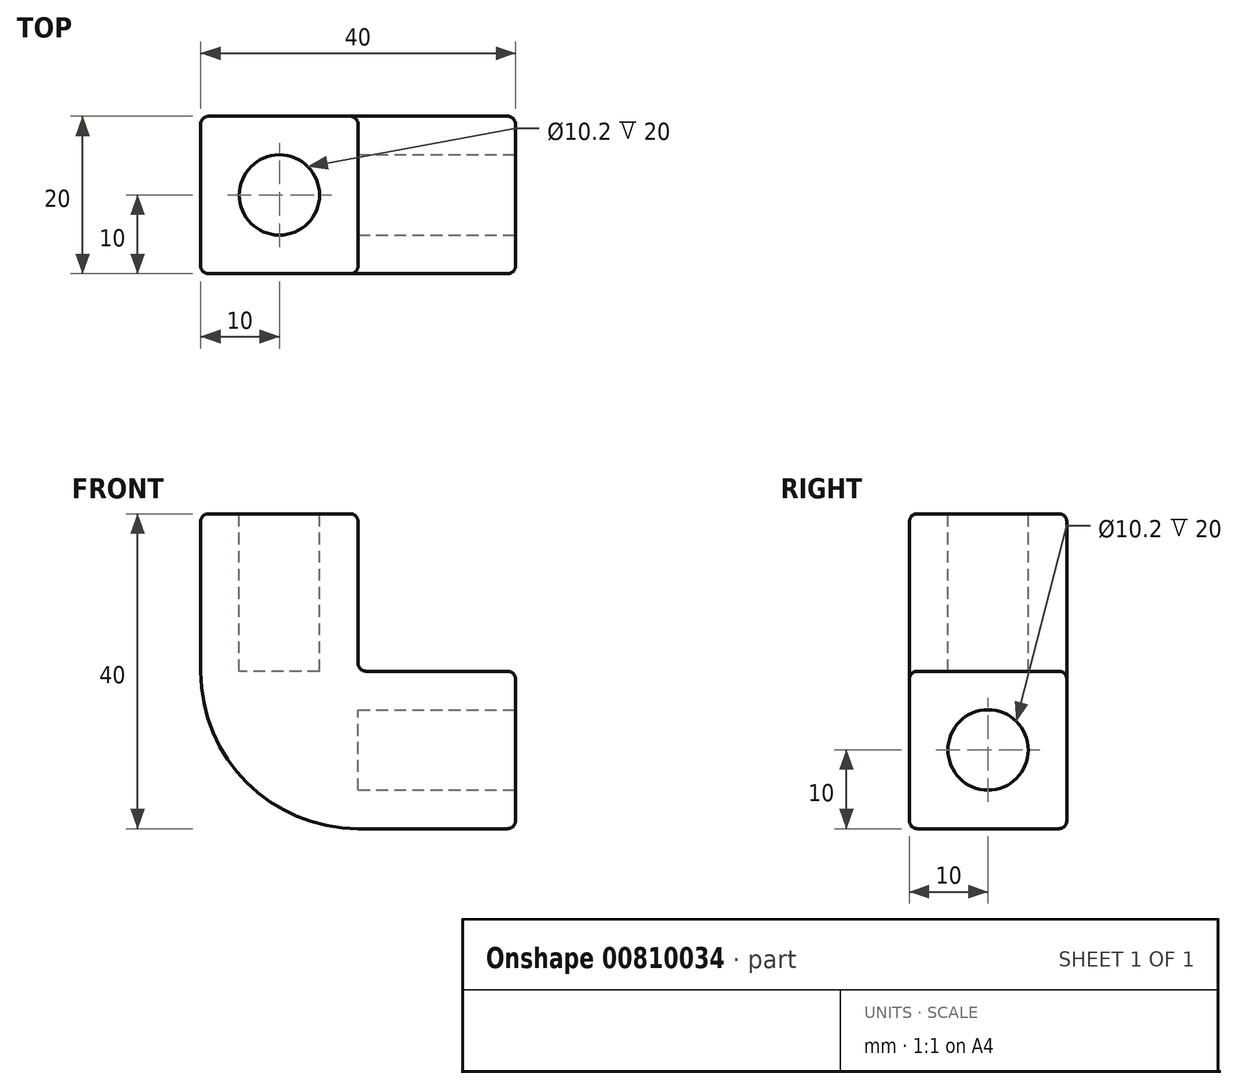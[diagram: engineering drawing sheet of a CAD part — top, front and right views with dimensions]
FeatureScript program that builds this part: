
annotation { "Feature Type Name" : "Feature", "Feature Type Description" : "" }
export const myFeature = defineFeature(function(context is Context, id is Id, definition is map)
    precondition{}
    {
        {
            var Q0;
            Q0=qCreatedBy(makeId("Front.planeOp"),FACE);
            var sketch = newSketch(context, id + "F0", { "sketchPlane" : qUnion([Q0])});
            skLineSegment(sketch, "E0.bottom", {"start": v(0, 0) * mm, "end": v(-20, 0) * mm});
            skLineSegment(sketch, "E0.top", {"start": v(0, 40) * mm, "end": v(-20, 40) * mm});
            skLineSegment(sketch, "E0.left", {"start": v(0, 0) * mm, "end": v(0, 40) * mm});
            skLineSegment(sketch, "E0.right", {"start": v(-20, 0) * mm, "end": v(-20, 40) * mm});
            skLineSegment(sketch, "E1.bottom", {"start": v(-20, 0) * mm, "end": v(20, 0) * mm});
            skLineSegment(sketch, "E1.top", {"start": v(-20, 20) * mm, "end": v(20, 20) * mm});
            skLineSegment(sketch, "E1.left", {"start": v(-20, 0) * mm, "end": v(-20, 20) * mm});
            skLineSegment(sketch, "E1.right", {"start": v(20, 0) * mm, "end": v(20, 20) * mm});
            skLineSegment(sketch, "E2", {"start": v(20, 20) * mm, "end": v(0, 40) * mm});
            skLineSegment(sketch, "E3", {"start": v(0, 0) * mm, "end": v(-20, 20) * mm});
            skArc(sketch, "E4", {"start": v(-20, 20) * mm, "mid": v(-14.14, 5.86) * mm, "end": v(0, 0) * mm});
            skArc(sketch, "E5", {"start": v(0, 40) * mm, "mid": v(5.86, 25.86) * mm, "end": v(20, 20) * mm});
            skSolve(sketch);
        }
        {
            var Q0;
            {var subQ0=sQuery(id+"F0.wireOp",EDGE,"E0.top");Q0=makeQuery(id+"F0.imprint","IMPRINT",FACE,{"disambiguationData":[TD([[makeQuery(id+"F0.imprint","IMPRINT",EDGE,{"derivedFrom":subQ0}),1.0]])]});}
            var Q1;
            {var subQ5=sQuery(id+"F0.wireOp",EDGE,"E1.right");Q1=makeQuery(id+"F0.imprint","IMPRINT",FACE,{"disambiguationData":[TD([[makeQuery(id+"F0.imprint","IMPRINT",EDGE,{"derivedFrom":subQ5}),1.0]])]});}
            var Q2;
            {var subQ0=sQuery(id+"F0.wireOp",EDGE,"E3");Q2=makeQuery(id+"F0.imprint","IMPRINT",FACE,{"disambiguationData":[TD([[makeQuery(id+"F0.imprint","IMPRINT",EDGE,{"derivedFrom":subQ0}),-1.0]])]});}
            var Q3;
            Q3=makeQuery(id+"F0.imprint","IMPRINT",FACE,{"disambiguationData":[TD([[makeQuery(id+"F0.imprint","IMPRINT",EDGE,{"derivedFrom":sQuery(id+"F0.wireOp",EDGE,"E3")}),1.0]])]});
            extrude(context, id + "F1", {"entities" : qUnion([Q0, Q1, Q2, Q3]), "depth" : 20 * mm, "offsetDistance" : 25 * mm});
        }
        {
            var Q0;
            Q0=makeQuery(id+"F1.opExtrude","CAP_EDGE",EDGE,{"disambiguationData":[OSD([sQuery(id+"F0.wireOp",EDGE,"E0.left")])],"isStart":false});
            var Q1;
            Q1=makeQuery(id+"F1.opExtrude","SWEPT_EDGE",EDGE,{"disambiguationData":[OSD([sQuery(id+"F0.wireOp",EDGE,"E0.top"),sQuery(id+"F0.wireOp",EDGE,"E0.left")])]});
            var Q2;
            Q2=makeQuery(id+"F1.opExtrude","CAP_EDGE",EDGE,{"disambiguationData":[OSD([sQuery(id+"F0.wireOp",EDGE,"E0.top")])],"isStart":false});
            var Q3;
            Q3=makeQuery(id+"F1.opExtrude","SWEPT_EDGE",EDGE,{"disambiguationData":[OSD([sQuery(id+"F0.wireOp",EDGE,"E0.top"),sQuery(id+"F0.wireOp",EDGE,"E0.right")])]});
            var Q4;
            Q4=makeQuery(id+"F1.opExtrude","CAP_EDGE",EDGE,{"disambiguationData":[OSD([sQuery(id+"F0.wireOp",EDGE,"E1.top")])],"isStart":false});
            var Q5;
            Q5=makeQuery(id+"F1.opExtrude","CAP_EDGE",EDGE,{"disambiguationData":[OSD([sQuery(id+"F0.wireOp",EDGE,"E1.top")])],"isStart":true});
            var Q6;
            Q6=makeQuery(id+"F1.opExtrude","SWEPT_EDGE",EDGE,{"disambiguationData":[OSD([sQuery(id+"F0.wireOp",EDGE,"E1.top"),sQuery(id+"F0.wireOp",EDGE,"E1.right")])]});
            var Q7;
            Q7=makeQuery(id+"F1.opExtrude","CAP_EDGE",EDGE,{"disambiguationData":[OSD([sQuery(id+"F0.wireOp",EDGE,"E1.right")])],"isStart":false});
            var Q8;
            Q8=makeQuery(id+"F1.opExtrude","CAP_EDGE",EDGE,{"disambiguationData":[OSD([sQuery(id+"F0.wireOp",EDGE,"E1.right")])],"isStart":true});
            var Q9;
            Q9=makeQuery(id+"F1.opExtrude","SWEPT_EDGE",EDGE,{"disambiguationData":[OSD([sQuery(id+"F0.wireOp",EDGE,"E1.bottom"),sQuery(id+"F0.wireOp",EDGE,"E1.right")])]});
            var Q10;
            Q10=makeQuery(id+"F1.opExtrude","CAP_EDGE",EDGE,{"disambiguationData":[OSD([sQuery(id+"F0.wireOp",EDGE,"E1.bottom")])],"isStart":false});
            var Q11;
            Q11=makeQuery(id+"F1.opExtrude","CAP_EDGE",EDGE,{"disambiguationData":[OSD([sQuery(id+"F0.wireOp",EDGE,"E0.right"),sQuery(id+"F0.wireOp",EDGE,"E1.left")])],"isStart":false});
            var Q12;
            Q12=makeQuery(id+"F1.opExtrude","CAP_EDGE",EDGE,{"disambiguationData":[OSD([sQuery(id+"F0.wireOp",EDGE,"E0.left")])],"isStart":true});
            var Q13;
            Q13=makeQuery(id+"F1.opExtrude","CAP_EDGE",EDGE,{"disambiguationData":[OSD([sQuery(id+"F0.wireOp",EDGE,"E0.top")])],"isStart":true});
            var Q14;
            Q14=makeQuery(id+"F1.opExtrude","CAP_EDGE",EDGE,{"disambiguationData":[OSD([sQuery(id+"F0.wireOp",EDGE,"E0.right"),sQuery(id+"F0.wireOp",EDGE,"E1.left")])],"isStart":true});
            var Q15;
            Q15=makeQuery(id+"F1.opExtrude","CAP_EDGE",EDGE,{"disambiguationData":[OSD([sQuery(id+"F0.wireOp",EDGE,"E1.bottom")])],"isStart":true});
            var Q16;
            Q16=makeQuery(id+"F1.opExtrude","SWEPT_EDGE",EDGE,{"disambiguationData":[OSD([sQuery(id+"F0.wireOp",EDGE,"E1.bottom"),sQuery(id+"F0.wireOp",EDGE,"E1.left")])]});
            var Q17;
            Q17=makeQuery(id+"F1.opExtrude","SWEPT_EDGE",EDGE,{"disambiguationData":[OSD([sQuery(id+"F0.wireOp",EDGE,"E0.left"),sQuery(id+"F0.wireOp",EDGE,"E1.top")])]});
            fillet(context, id + "F2", {"entities" : qUnion([Q0, Q1, Q2, Q3, Q4, Q5, Q6, Q7, Q8, Q9, Q10, Q11, Q12, Q13, Q14, Q15, Q16, Q17]), "radius" : 1 * mm, "tangentPropagation" : true, "allowEdgeOverflow" : false});
        }
        {
            var Q0;
            Q0=makeQuery(id+"F1.opExtrude","SWEPT_FACE",FACE,{"disambiguationData":[OSD([sQuery(id+"F0.wireOp",EDGE,"E0.top")])]});
            var sketch = newSketch(context, id + "F3", { "sketchPlane" : qUnion([Q0])});
            skCircle(sketch, "E6", {"center": v(-10, -10) * mm, "radius": 5.1 * mm});
            skPoint(sketch, "E6.centerSnap0", {"position": v(-10, -1) * mm});
            skPoint(sketch, "E6.centerSnap1", {"position": v(-1, -10) * mm});
            skSolve(sketch);
        }
        {
            var Q0;
            Q0=makeQuery(id+"F3.imprint","IMPRINT",FACE,{"disambiguationData":[TD([[makeQuery(id+"F3.imprint","IMPRINT",EDGE,{"derivedFrom":sQuery(id+"F3.wireOp",EDGE,"E6")}),1.0]])]});
            extrude(context, id + "F4", {"entities" : qUnion([Q0]), "operationType" : NewBodyOperationType.REMOVE, "oppositeDirection" : true, "depth" : 20 * mm, "offsetDistance" : 25 * mm});
        }
        {
            var Q0;
            Q0=makeQuery(id+"F1.opExtrude","SWEPT_FACE",FACE,{"disambiguationData":[OSD([sQuery(id+"F0.wireOp",EDGE,"E1.right")])]});
            var sketch = newSketch(context, id + "F5", { "sketchPlane" : qUnion([Q0])});
            skCircle(sketch, "E7", {"center": v(-10, 10) * mm, "radius": 5.1 * mm});
            skPoint(sketch, "E7.centerSnap0", {"position": v(-1, 10) * mm});
            skPoint(sketch, "E7.centerSnap1", {"position": v(-10, 19) * mm});
            skSolve(sketch);
        }
        {
            var Q0;
            Q0=makeQuery(id+"F5.imprint","IMPRINT",FACE,{"disambiguationData":[TD([[makeQuery(id+"F5.imprint","IMPRINT",EDGE,{"derivedFrom":sQuery(id+"F5.wireOp",EDGE,"E7")}),1.0]])]});
            extrude(context, id + "F6", {"entities" : qUnion([Q0]), "operationType" : NewBodyOperationType.REMOVE, "oppositeDirection" : true, "depth" : 20 * mm, "offsetDistance" : 25 * mm});
        }
    });
